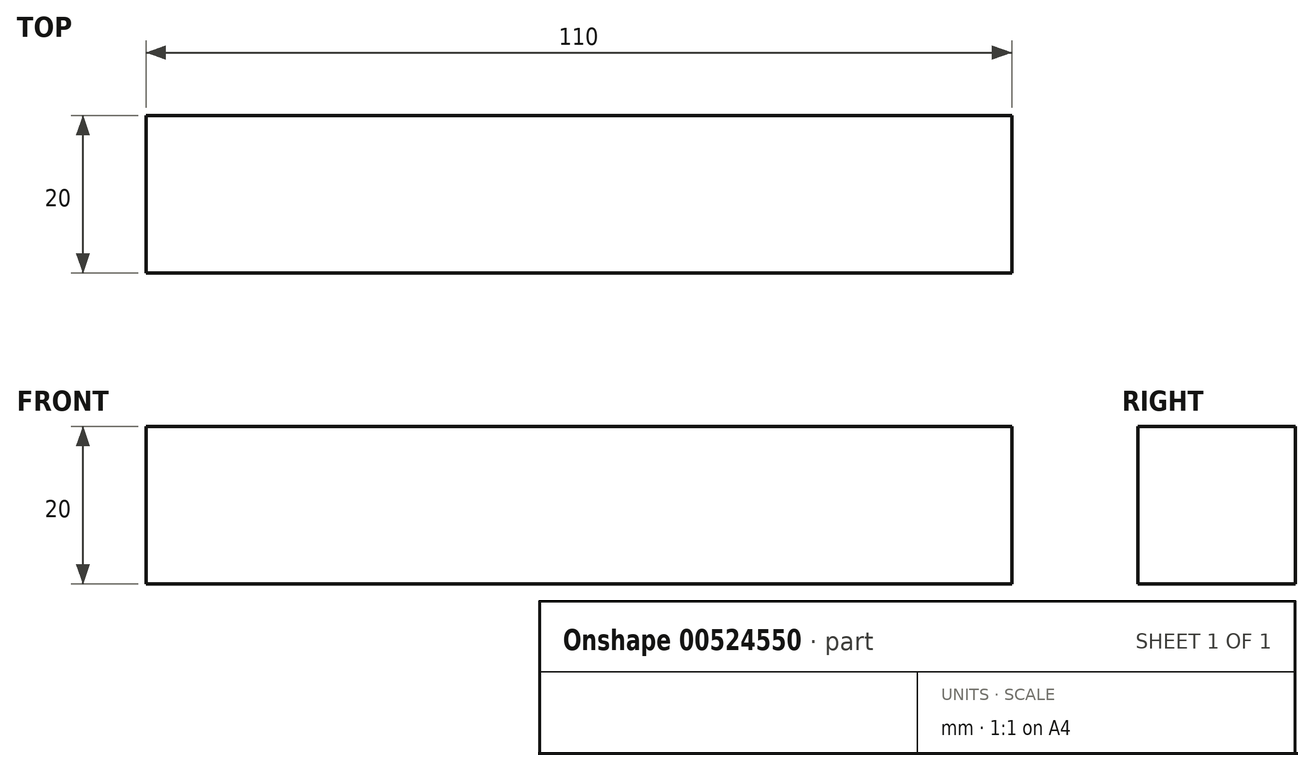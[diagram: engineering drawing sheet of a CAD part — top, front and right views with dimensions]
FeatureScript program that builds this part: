
annotation { "Feature Type Name" : "Feature", "Feature Type Description" : "" }
export const myFeature = defineFeature(function(context is Context, id is Id, definition is map)
    precondition{}
    {
        {
            var Q0;
            Q0=qCreatedBy(makeId("Front.planeOp"),FACE);
            var sketch = newSketch(context, id + "F0", { "sketchPlane" : qUnion([Q0])});
            skLineSegment(sketch, "E0.bottom", {"start": v(0, 0) * mm, "end": v(110, 0) * mm});
            skLineSegment(sketch, "E0.top", {"start": v(0, 20) * mm, "end": v(110, 20) * mm});
            skLineSegment(sketch, "E0.left", {"start": v(0, 0) * mm, "end": v(0, 20) * mm});
            skLineSegment(sketch, "E0.right", {"start": v(110, 0) * mm, "end": v(110, 20) * mm});
            skSolve(sketch);
        }
        {
            var Q0;
            Q0=makeQuery(id+"F0.imprint","IMPRINT",FACE,{"disambiguationData":[TD([[makeQuery(id+"F0.imprint","IMPRINT",EDGE,{"derivedFrom":sQuery(id+"F0.wireOp",EDGE,"E0.bottom")}),1.0]])]});
            extrude(context, id + "F1", {"entities" : qUnion([Q0]), "depth" : 20 * mm, "offsetDistance" : 25.4 * mm});
        }
    });
